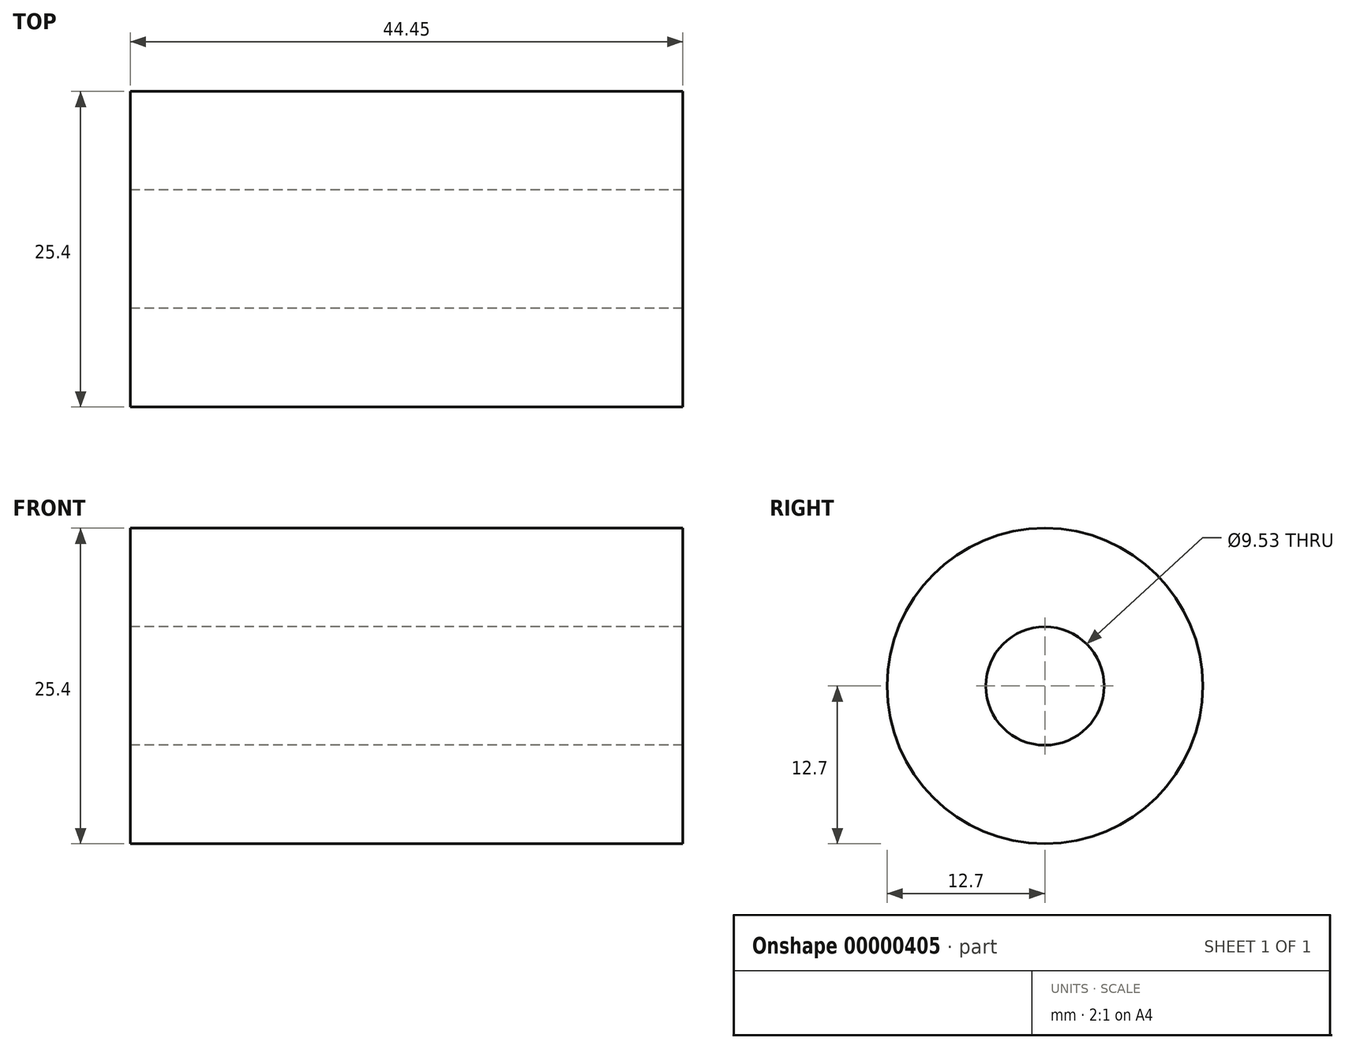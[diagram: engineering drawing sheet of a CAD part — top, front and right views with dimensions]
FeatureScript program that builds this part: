
annotation { "Feature Type Name" : "Feature", "Feature Type Description" : "" }
export const myFeature = defineFeature(function(context is Context, id is Id, definition is map)
    precondition{}
    {
        {
            var Q0;
            Q0=qCreatedBy(makeId("Right.planeOp"),FACE);
            var sketch = newSketch(context, id + "F0", { "sketchPlane" : qUnion([Q0])});
            skCircle(sketch, "E0", {"center": v(0, 0) * mm, "radius": 12.7 * mm});
            skCircle(sketch, "E1", {"center": v(0, 0) * mm, "radius": 4.76 * mm});
            skSolve(sketch);
        }
        {
            var Q0;
            Q0 = qSketchRegion(id + "F0", true);
            extrude(context, id + "F1", {"entities" : qUnion([Q0]), "depth" : 44.45 * mm});
        }
    });
